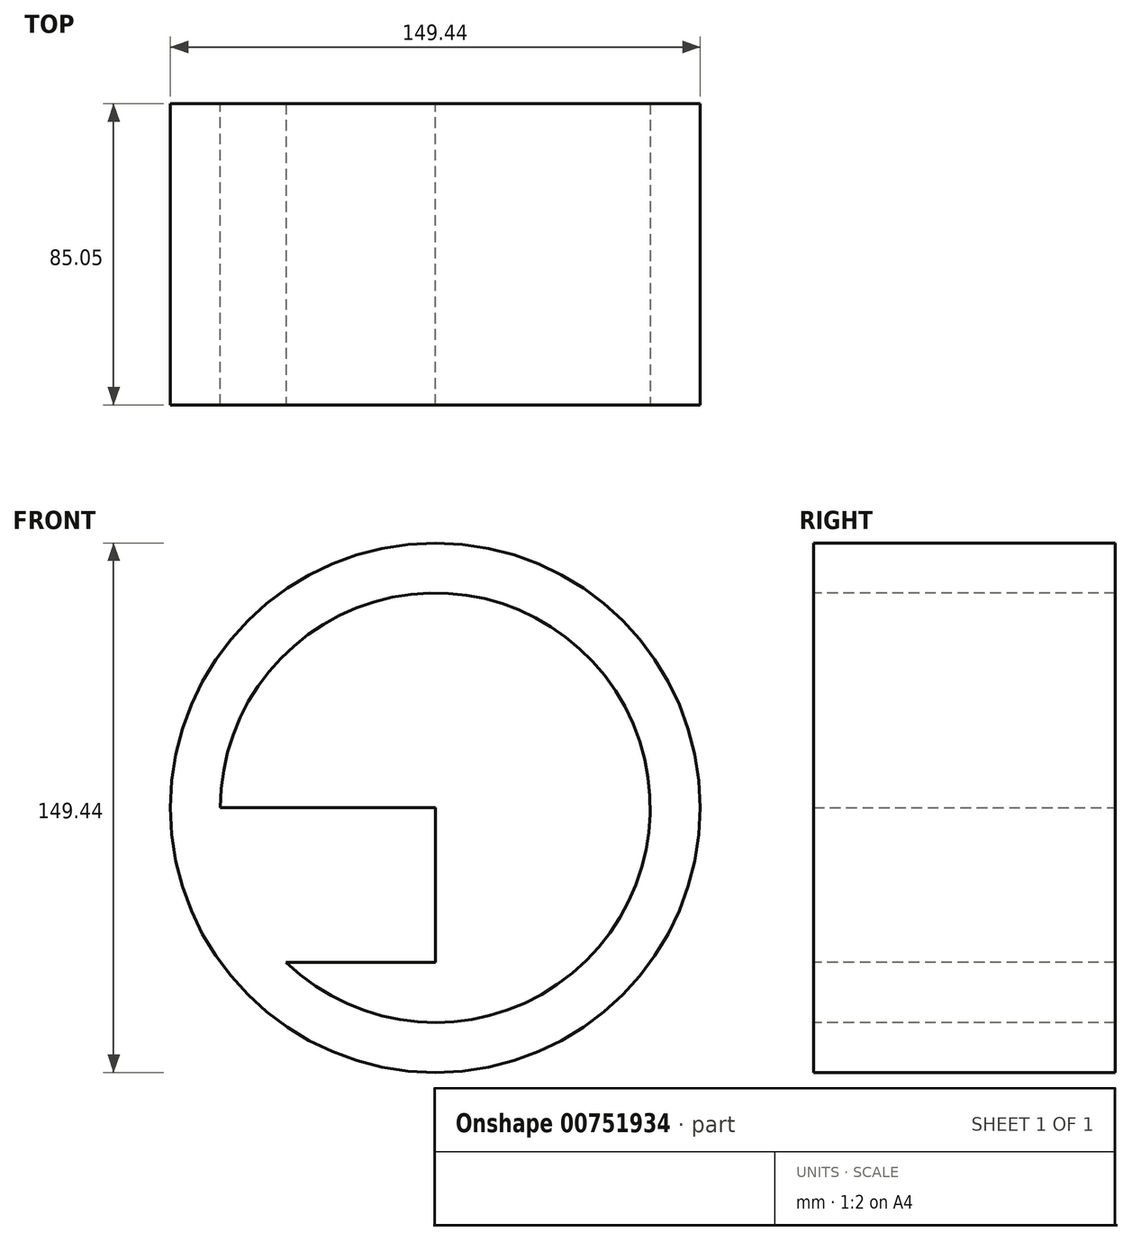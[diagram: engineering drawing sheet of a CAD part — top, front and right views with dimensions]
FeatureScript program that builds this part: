
annotation { "Feature Type Name" : "Feature", "Feature Type Description" : "" }
export const myFeature = defineFeature(function(context is Context, id is Id, definition is map)
    precondition{}
    {
        {
            var Q0;
            Q0=qCreatedBy(makeId("Front.planeOp"),FACE);
            var sketch = newSketch(context, id + "F0", { "sketchPlane" : qUnion([Q0])});
            skLineSegment(sketch, "E0.bottom", {"start": v(34.65, 0) * mm, "end": v(0, 0) * mm});
            skLineSegment(sketch, "E0.top", {"start": v(34.65, -44.75) * mm, "end": v(0, -44.75) * mm});
            skLineSegment(sketch, "E0.left", {"start": v(34.65, 0) * mm, "end": v(34.65, -44.75) * mm});
            skLineSegment(sketch, "E0.right", {"start": v(0, 0) * mm, "end": v(0, -44.75) * mm});
            skLineSegment(sketch, "E1.bottom", {"start": v(24.36, 9.56) * mm, "end": v(-36.27, 9.56) * mm});
            skLineSegment(sketch, "E1.top", {"start": v(24.36, 53.23) * mm, "end": v(-36.27, 53.23) * mm});
            skLineSegment(sketch, "E1.left", {"start": v(24.36, 9.56) * mm, "end": v(24.36, 53.23) * mm});
            skLineSegment(sketch, "E1.right", {"start": v(-36.27, 9.56) * mm, "end": v(-36.27, 53.23) * mm});
            skLineSegment(sketch, "E2", {"start": v(44.57, 63.52) * mm, "end": v(24.36, 53.6) * mm});
            skLineSegment(sketch, "E3", {"start": v(24.36, 53.6) * mm, "end": v(25.98, 11.37) * mm});
            skLineSegment(sketch, "E4", {"start": v(25.98, 11.37) * mm, "end": v(54.67, 37.17) * mm});
            skLineSegment(sketch, "E5", {"start": v(54.67, 37.17) * mm, "end": v(44.57, 63.52) * mm});
            skLineSegment(sketch, "E6", {"start": v(44.75, 64.78) * mm, "end": v(-36.27, 53.23) * mm});
            skLineSegment(sketch, "E7", {"start": v(10.29, 14.62) * mm, "end": v(10.29, -44.75) * mm});
            skLineSegment(sketch, "E8", {"start": v(10.29, -44.75) * mm, "end": v(54.67, 37.17) * mm});
            skSolve(sketch);
        }
        {
            var Q0;
            Q0=makeQuery(id+"F0.imprint","IMPRINT",FACE,{"disambiguationData":[TD([[makeQuery(id+"F0.imprint","IMPRINT",EDGE,{"derivedFrom":sQuery(id+"F0.wireOp",EDGE,"E1.top")}),1.0]])]});
            extrude(context, id + "F1", {"entities" : qUnion([Q0]), "depth" : 85.05 * mm, "offsetDistance" : 25.4 * mm});
        }
        {
            var Q0;
            Q0=makeQuery(id+"F1.opExtrude","SWEPT_FACE",FACE,{"disambiguationData":[OSD([sQuery(id+"F0.wireOp",EDGE,"E1.right")])]});
            var Q1;
            Q1=makeQuery(id+"F1.opExtrude","SWEPT_EDGE",EDGE,{"disambiguationData":[OSD([sQuery(id+"F0.wireOp",EDGE,"E1.top"),sQuery(id+"F0.wireOp",EDGE,"E1.left")])]});
            revolve(context, id + "F2", {"operationType" : NewBodyOperationType.ADD, "surfaceOperationType" : NewSurfaceOperationType.NEW, "entities" : qUnion([Q0]), "axis" : qUnion([Q1]), "revolveType" : RevolveType.FULL});
        }
    });
